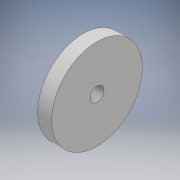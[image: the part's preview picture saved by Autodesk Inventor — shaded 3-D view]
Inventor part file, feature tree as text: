
AUTODESK INVENTOR PART (.ipt)
format: ipt  version: 2018 (Build 220112000, 112)  size: 93,696 bytes
history: native  units: mm
features: other x1, extrude x1, sketch x1
ambient origin geometry x8: Origin, YZ Plane, XZ Plane, XY Plane, X Axis, Y Axis, Z Axis, Center Point
bodies: Body1 (feature_tree)
feature tree (3):
  other  "Sólido1"
  extrude  "Extrusión1"  [1 undecoded]
  sketch  "Boceto1"  dims[d2=3.0mm d3=0.0mm]
note: 1 required parameter value undecoded (feature->parameter linkage not recoverable at this tier; creation-order binding heuristic only, values carry confidence <= 0.55)
